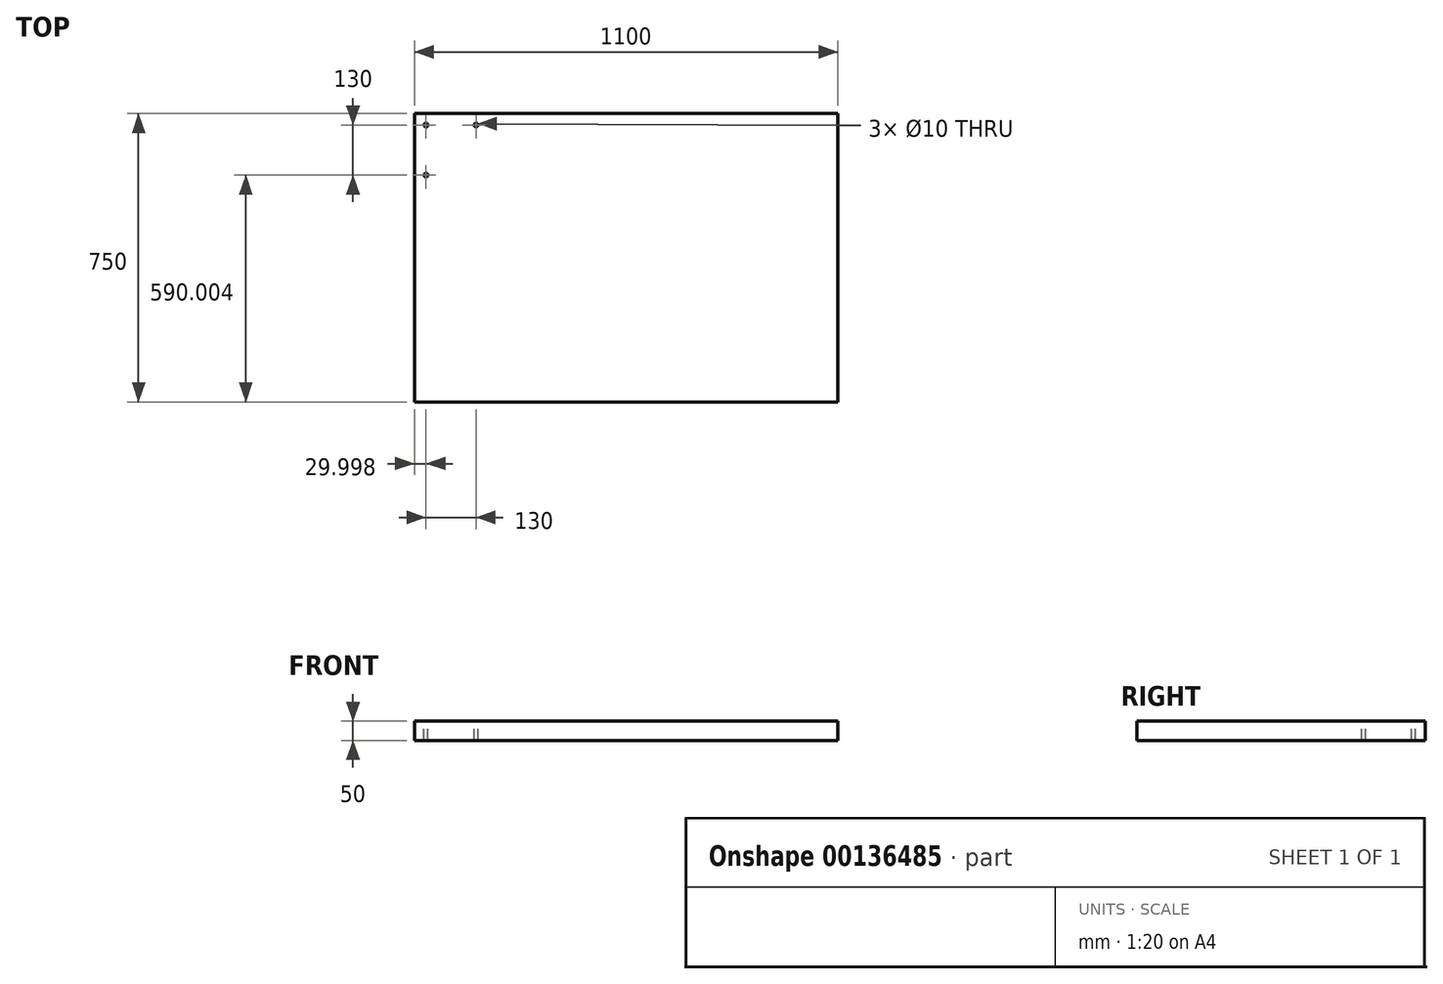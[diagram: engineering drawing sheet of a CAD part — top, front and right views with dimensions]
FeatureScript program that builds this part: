
annotation { "Feature Type Name" : "Feature", "Feature Type Description" : "" }
export const myFeature = defineFeature(function(context is Context, id is Id, definition is map)
    precondition{}
    {
        {
            var Q0;
            Q0=qCreatedBy(makeId("Top.planeOp"),FACE);
            var sketch = newSketch(context, id + "F0", { "sketchPlane" : qUnion([Q0])});
            skLineSegment(sketch, "E0.bottom", {"start": v(-527.93, 526.8) * mm, "end": v(572.07, 526.8) * mm});
            skLineSegment(sketch, "E0.top", {"start": v(-527.93, -223.2) * mm, "end": v(572.07, -223.2) * mm});
            skLineSegment(sketch, "E0.left", {"start": v(-527.93, 526.8) * mm, "end": v(-527.93, -223.2) * mm});
            skLineSegment(sketch, "E0.right", {"start": v(572.07, 526.8) * mm, "end": v(572.07, -223.2) * mm});
            skSolve(sketch);
        }
        {
            var Q0;
            Q0 = qSketchRegion(id + "F0", true);
            extrude(context, id + "F1", {"entities" : qUnion([Q0]), "depth" : 50 * mm});
        }
        {
            var Q0;
            Q0=makeQuery(id+"F1.opExtrude","CAP_FACE",FACE,{"disambiguationData":[OSD([sQuery(id+"F0.wireOp",EDGE,"E0.bottom"),sQuery(id+"F0.wireOp",EDGE,"E0.top"),sQuery(id+"F0.wireOp",EDGE,"E0.left"),sQuery(id+"F0.wireOp",EDGE,"E0.right")])],"isStart":false});
            var sketch = newSketch(context, id + "F2", { "sketchPlane" : qUnion([Q0])});
            skCircle(sketch, "E1", {"center": v(-497.93, 496.8) * mm, "radius": 5 * mm});
            skCircle(sketch, "E2.0.1.0", {"center": v(-497.93, 366.8) * mm, "radius": 5 * mm});
            skCircle(sketch, "E2.1.0.0", {"center": v(-367.93, 496.8) * mm, "radius": 5 * mm});
            skCircle(sketch, "E2.1.1.0", {"center": v(-367.93, 366.8) * mm, "radius": 5 * mm});
            skLineSegment(sketch, "E2.direction1", {"start": v(-497.93, 496.8) * mm, "end": v(-367.93, 496.8) * mm, "construction": true});
            skLineSegment(sketch, "E2.direction2", {"start": v(-497.93, 496.8) * mm, "end": v(-497.93, 366.8) * mm, "construction": true});
            skSolve(sketch);
        }
        {
            var Q0;
            Q0=makeQuery(id+"F2.imprint","IMPRINT",FACE,{"disambiguationData":[TD([[makeQuery(id+"F2.imprint","IMPRINT",EDGE,{"derivedFrom":sQuery(id+"F2.wireOp",EDGE,"E1")}),1.0]])]});
            var Q1;
            Q1=makeQuery(id+"F2.imprint","IMPRINT",FACE,{"disambiguationData":[TD([[makeQuery(id+"F2.imprint","IMPRINT",EDGE,{"derivedFrom":sQuery(id+"F2.wireOp",EDGE,"E2.1.0.0")}),1.0]])]});
            var Q2;
            Q2=makeQuery(id+"F2.imprint","IMPRINT",FACE,{"disambiguationData":[TD([[makeQuery(id+"F2.imprint","IMPRINT",EDGE,{"derivedFrom":sQuery(id+"F2.wireOp",EDGE,"E2.0.1.0")}),1.0]])]});
            extrude(context, id + "F3", {"entities" : qUnion([Q0, Q1, Q2]), "operationType" : NewBodyOperationType.REMOVE, "endBound" : BoundingType.THROUGH_ALL, "oppositeDirection" : true, "depth" : 25 * mm});
        }
    });
